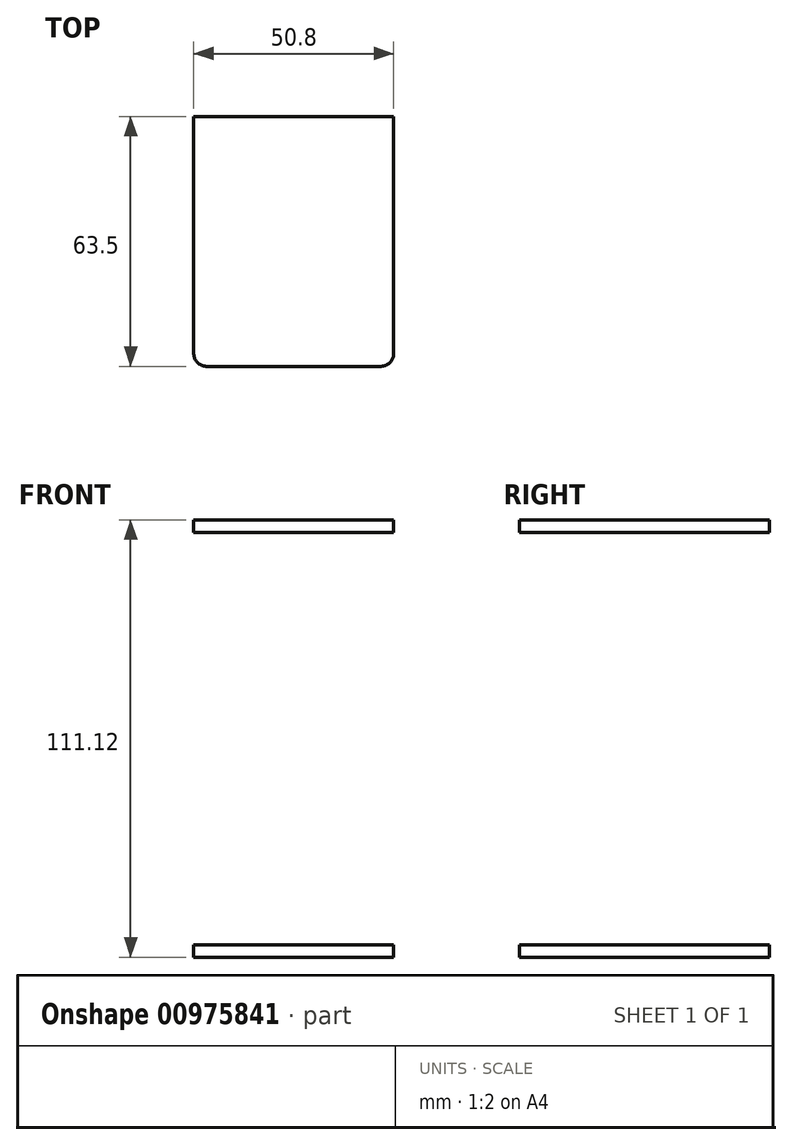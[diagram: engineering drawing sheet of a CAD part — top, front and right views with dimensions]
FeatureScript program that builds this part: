
annotation { "Feature Type Name" : "Feature", "Feature Type Description" : "" }
export const myFeature = defineFeature(function(context is Context, id is Id, definition is map)
    precondition{}
    {
        {
            var Q0;
            Q0=qCreatedBy(makeId("Front.planeOp"),FACE);
            var sketch = newSketch(context, id + "F0", { "sketchPlane" : qUnion([Q0])});
            skLineSegment(sketch, "E0.bottom", {"start": v(-72.27, 0) * mm, "end": v(-21.47, 0) * mm});
            skLineSegment(sketch, "E0.top", {"start": v(-72.27, -3.18) * mm, "end": v(-21.47, -3.18) * mm});
            skLineSegment(sketch, "E0.left", {"start": v(-72.27, 0) * mm, "end": v(-72.27, -3.18) * mm});
            skLineSegment(sketch, "E0.right", {"start": v(-21.47, 0) * mm, "end": v(-21.47, -3.18) * mm});
            skSolve(sketch);
        }
        {
            var Q0;
            Q0=qSketchRegion(id+"F0",true);
            extrude(context, id + "F1", {"entities" : qUnion([Q0]), "depth" : 63.5 * mm, "offsetDistance" : 25.4 * mm});
        }
        {
            var Q0;
            Q0=makeQuery(id+"F1.opExtrude","CAP_EDGE",EDGE,{"disambiguationData":[OSD([sQuery(id+"F0.wireOp",EDGE,"E0.right")])],"isStart":false});
            fillet(context, id + "F2", {"entities" : qUnion([Q0]), "radius" : 3.17 * mm, "tangentPropagation" : true, "allowEdgeOverflow" : false});
        }
        {
            var Q0;
            Q0=makeQuery(id+"F1.opExtrude","CAP_EDGE",EDGE,{"disambiguationData":[OSD([sQuery(id+"F0.wireOp",EDGE,"E0.left")])],"isStart":false});
            fillet(context, id + "F3", {"entities" : qUnion([Q0]), "radius" : 3.17 * mm, "tangentPropagation" : true, "allowEdgeOverflow" : false});
        }
        {
            var Q0;
            Q0=makeQuery(id+"F1.opExtrude","SWEPT_BODY",BODY,{"disambiguationData":[OSD([sQuery(id+"F0.wireOp",EDGE,"E0.bottom"),sQuery(id+"F0.wireOp",EDGE,"E0.top"),sQuery(id+"F0.wireOp",EDGE,"E0.left"),sQuery(id+"F0.wireOp",EDGE,"E0.right")])]});
            transform(context, id + "F4", {"entities" : qUnion([Q0]), "transformType" : TransformType.TRANSLATION_3D, "dx" : 76.2 * mm, "dy" : 0 * mm, "dz" : 0 * mm, "makeCopy" : true});
        }
        {
            var Q0;
            Q0=makeQuery(id+"F4.opPattern","COPY",BODY,{"derivedFrom":makeQuery(id+"F1.opExtrude","SWEPT_BODY",BODY,{"disambiguationData":[OSD([sQuery(id+"F0.wireOp",EDGE,"E0.bottom"),sQuery(id+"F0.wireOp",EDGE,"E0.top"),sQuery(id+"F0.wireOp",EDGE,"E0.left"),sQuery(id+"F0.wireOp",EDGE,"E0.right")])]}),"instanceName":"1"});
            transform(context, id + "F5", {"entities" : qUnion([Q0]), "transformType" : TransformType.TRANSLATION_3D, "dx" : 76.2 * mm, "dy" : 0 * mm, "dz" : 0 * mm, "makeCopy" : true});
        }
        {
            var Q0;
            Q0=makeQuery(id+"F5.opPattern","COPY",BODY,{"derivedFrom":makeQuery(id+"F4.opPattern","COPY",BODY,{"derivedFrom":makeQuery(id+"F1.opExtrude","SWEPT_BODY",BODY,{"disambiguationData":[OSD([sQuery(id+"F0.wireOp",EDGE,"E0.bottom"),sQuery(id+"F0.wireOp",EDGE,"E0.top"),sQuery(id+"F0.wireOp",EDGE,"E0.left"),sQuery(id+"F0.wireOp",EDGE,"E0.right")])]}),"instanceName":"1"}),"instanceName":"1"});
            transform(context, id + "F6", {"entities" : qUnion([Q0]), "transformType" : TransformType.TRANSLATION_3D, "dx" : 76.2 * mm, "dy" : 0 * mm, "dz" : 0 * mm, "makeCopy" : true});
        }
        {
            var Q0;
            Q0=makeQuery(id+"F6.opPattern","COPY",BODY,{"derivedFrom":makeQuery(id+"F5.opPattern","COPY",BODY,{"derivedFrom":makeQuery(id+"F4.opPattern","COPY",BODY,{"derivedFrom":makeQuery(id+"F1.opExtrude","SWEPT_BODY",BODY,{"disambiguationData":[OSD([sQuery(id+"F0.wireOp",EDGE,"E0.bottom"),sQuery(id+"F0.wireOp",EDGE,"E0.top"),sQuery(id+"F0.wireOp",EDGE,"E0.left"),sQuery(id+"F0.wireOp",EDGE,"E0.right")])]}),"instanceName":"1"}),"instanceName":"1"}),"instanceName":"1"});
            transform(context, id + "F7", {"entities" : qUnion([Q0]), "transformType" : TransformType.TRANSLATION_3D, "dx" : 76.2 * mm, "dy" : 0 * mm, "dz" : 0 * mm, "makeCopy" : true});
        }
        {
            var Q0;
            Q0=makeQuery(id+"F1.opExtrude","SWEPT_BODY",BODY,{"disambiguationData":[OSD([sQuery(id+"F0.wireOp",EDGE,"E0.bottom"),sQuery(id+"F0.wireOp",EDGE,"E0.top"),sQuery(id+"F0.wireOp",EDGE,"E0.left"),sQuery(id+"F0.wireOp",EDGE,"E0.right")])]});
            var Q1;
            Q1=makeQuery(id+"F4.opPattern","COPY",BODY,{"derivedFrom":makeQuery(id+"F1.opExtrude","SWEPT_BODY",BODY,{"disambiguationData":[OSD([sQuery(id+"F0.wireOp",EDGE,"E0.bottom"),sQuery(id+"F0.wireOp",EDGE,"E0.top"),sQuery(id+"F0.wireOp",EDGE,"E0.left"),sQuery(id+"F0.wireOp",EDGE,"E0.right")])]}),"instanceName":"1"});
            var Q2;
            Q2=makeQuery(id+"F5.opPattern","COPY",BODY,{"derivedFrom":makeQuery(id+"F4.opPattern","COPY",BODY,{"derivedFrom":makeQuery(id+"F1.opExtrude","SWEPT_BODY",BODY,{"disambiguationData":[OSD([sQuery(id+"F0.wireOp",EDGE,"E0.bottom"),sQuery(id+"F0.wireOp",EDGE,"E0.top"),sQuery(id+"F0.wireOp",EDGE,"E0.left"),sQuery(id+"F0.wireOp",EDGE,"E0.right")])]}),"instanceName":"1"}),"instanceName":"1"});
            var Q3;
            Q3=makeQuery(id+"F6.opPattern","COPY",BODY,{"derivedFrom":makeQuery(id+"F5.opPattern","COPY",BODY,{"derivedFrom":makeQuery(id+"F4.opPattern","COPY",BODY,{"derivedFrom":makeQuery(id+"F1.opExtrude","SWEPT_BODY",BODY,{"disambiguationData":[OSD([sQuery(id+"F0.wireOp",EDGE,"E0.bottom"),sQuery(id+"F0.wireOp",EDGE,"E0.top"),sQuery(id+"F0.wireOp",EDGE,"E0.left"),sQuery(id+"F0.wireOp",EDGE,"E0.right")])]}),"instanceName":"1"}),"instanceName":"1"}),"instanceName":"1"});
            var Q4;
            Q4=makeQuery(id+"F7.opPattern","COPY",BODY,{"derivedFrom":makeQuery(id+"F6.opPattern","COPY",BODY,{"derivedFrom":makeQuery(id+"F5.opPattern","COPY",BODY,{"derivedFrom":makeQuery(id+"F4.opPattern","COPY",BODY,{"derivedFrom":makeQuery(id+"F1.opExtrude","SWEPT_BODY",BODY,{"disambiguationData":[OSD([sQuery(id+"F0.wireOp",EDGE,"E0.bottom"),sQuery(id+"F0.wireOp",EDGE,"E0.top"),sQuery(id+"F0.wireOp",EDGE,"E0.left"),sQuery(id+"F0.wireOp",EDGE,"E0.right")])]}),"instanceName":"1"}),"instanceName":"1"}),"instanceName":"1"}),"instanceName":"1"});
            transform(context, id + "F8", {"entities" : qUnion([Q0, Q1, Q2, Q3, Q4]), "transformType" : TransformType.TRANSLATION_3D, "dx" : 0 * mm, "dy" : 0 * mm, "dz" : 104.77 * mm, "makeCopy" : true});
        }
        {
            var Q0;
            Q0=makeQuery(id+"F8.opPattern","COPY",BODY,{"derivedFrom":makeQuery(id+"F1.opExtrude","SWEPT_BODY",BODY,{"disambiguationData":[OSD([sQuery(id+"F0.wireOp",EDGE,"E0.bottom"),sQuery(id+"F0.wireOp",EDGE,"E0.top"),sQuery(id+"F0.wireOp",EDGE,"E0.left"),sQuery(id+"F0.wireOp",EDGE,"E0.right")])]}),"instanceName":"1"});
            var Q1;
            Q1=makeQuery(id+"F8.opPattern","COPY",BODY,{"derivedFrom":makeQuery(id+"F4.opPattern","COPY",BODY,{"derivedFrom":makeQuery(id+"F1.opExtrude","SWEPT_BODY",BODY,{"disambiguationData":[OSD([sQuery(id+"F0.wireOp",EDGE,"E0.bottom"),sQuery(id+"F0.wireOp",EDGE,"E0.top"),sQuery(id+"F0.wireOp",EDGE,"E0.left"),sQuery(id+"F0.wireOp",EDGE,"E0.right")])]}),"instanceName":"1"}),"instanceName":"1"});
            var Q2;
            Q2=makeQuery(id+"F8.opPattern","COPY",BODY,{"derivedFrom":makeQuery(id+"F6.opPattern","COPY",BODY,{"derivedFrom":makeQuery(id+"F5.opPattern","COPY",BODY,{"derivedFrom":makeQuery(id+"F4.opPattern","COPY",BODY,{"derivedFrom":makeQuery(id+"F1.opExtrude","SWEPT_BODY",BODY,{"disambiguationData":[OSD([sQuery(id+"F0.wireOp",EDGE,"E0.bottom"),sQuery(id+"F0.wireOp",EDGE,"E0.top"),sQuery(id+"F0.wireOp",EDGE,"E0.left"),sQuery(id+"F0.wireOp",EDGE,"E0.right")])]}),"instanceName":"1"}),"instanceName":"1"}),"instanceName":"1"}),"instanceName":"1"});
            var Q3;
            Q3=makeQuery(id+"F8.opPattern","COPY",BODY,{"derivedFrom":makeQuery(id+"F7.opPattern","COPY",BODY,{"derivedFrom":makeQuery(id+"F6.opPattern","COPY",BODY,{"derivedFrom":makeQuery(id+"F5.opPattern","COPY",BODY,{"derivedFrom":makeQuery(id+"F4.opPattern","COPY",BODY,{"derivedFrom":makeQuery(id+"F1.opExtrude","SWEPT_BODY",BODY,{"disambiguationData":[OSD([sQuery(id+"F0.wireOp",EDGE,"E0.bottom"),sQuery(id+"F0.wireOp",EDGE,"E0.top"),sQuery(id+"F0.wireOp",EDGE,"E0.left"),sQuery(id+"F0.wireOp",EDGE,"E0.right")])]}),"instanceName":"1"}),"instanceName":"1"}),"instanceName":"1"}),"instanceName":"1"}),"instanceName":"1"});
            var Q4;
            Q4=makeQuery(id+"F8.opPattern","COPY",BODY,{"derivedFrom":makeQuery(id+"F5.opPattern","COPY",BODY,{"derivedFrom":makeQuery(id+"F4.opPattern","COPY",BODY,{"derivedFrom":makeQuery(id+"F1.opExtrude","SWEPT_BODY",BODY,{"disambiguationData":[OSD([sQuery(id+"F0.wireOp",EDGE,"E0.bottom"),sQuery(id+"F0.wireOp",EDGE,"E0.top"),sQuery(id+"F0.wireOp",EDGE,"E0.left"),sQuery(id+"F0.wireOp",EDGE,"E0.right")])]}),"instanceName":"1"}),"instanceName":"1"}),"instanceName":"1"});
            transform(context, id + "F9", {"entities" : qUnion([Q0, Q1, Q2, Q3, Q4]), "transformType" : TransformType.TRANSLATION_3D, "dx" : 0 * mm, "dy" : 0 * mm, "dz" : 127 * mm, "makeCopy" : true});
        }
        {
            var Q0;
            Q0=makeQuery(id+"F9.opPattern","COPY",BODY,{"derivedFrom":makeQuery(id+"F8.opPattern","COPY",BODY,{"derivedFrom":makeQuery(id+"F1.opExtrude","SWEPT_BODY",BODY,{"disambiguationData":[OSD([sQuery(id+"F0.wireOp",EDGE,"E0.bottom"),sQuery(id+"F0.wireOp",EDGE,"E0.top"),sQuery(id+"F0.wireOp",EDGE,"E0.left"),sQuery(id+"F0.wireOp",EDGE,"E0.right")])]}),"instanceName":"1"}),"instanceName":"1"});
            var Q1;
            Q1=makeQuery(id+"F9.opPattern","COPY",BODY,{"derivedFrom":makeQuery(id+"F8.opPattern","COPY",BODY,{"derivedFrom":makeQuery(id+"F4.opPattern","COPY",BODY,{"derivedFrom":makeQuery(id+"F1.opExtrude","SWEPT_BODY",BODY,{"disambiguationData":[OSD([sQuery(id+"F0.wireOp",EDGE,"E0.bottom"),sQuery(id+"F0.wireOp",EDGE,"E0.top"),sQuery(id+"F0.wireOp",EDGE,"E0.left"),sQuery(id+"F0.wireOp",EDGE,"E0.right")])]}),"instanceName":"1"}),"instanceName":"1"}),"instanceName":"1"});
            var Q2;
            Q2=makeQuery(id+"F9.opPattern","COPY",BODY,{"derivedFrom":makeQuery(id+"F8.opPattern","COPY",BODY,{"derivedFrom":makeQuery(id+"F5.opPattern","COPY",BODY,{"derivedFrom":makeQuery(id+"F4.opPattern","COPY",BODY,{"derivedFrom":makeQuery(id+"F1.opExtrude","SWEPT_BODY",BODY,{"disambiguationData":[OSD([sQuery(id+"F0.wireOp",EDGE,"E0.bottom"),sQuery(id+"F0.wireOp",EDGE,"E0.top"),sQuery(id+"F0.wireOp",EDGE,"E0.left"),sQuery(id+"F0.wireOp",EDGE,"E0.right")])]}),"instanceName":"1"}),"instanceName":"1"}),"instanceName":"1"}),"instanceName":"1"});
            var Q3;
            Q3=makeQuery(id+"F9.opPattern","COPY",BODY,{"derivedFrom":makeQuery(id+"F8.opPattern","COPY",BODY,{"derivedFrom":makeQuery(id+"F6.opPattern","COPY",BODY,{"derivedFrom":makeQuery(id+"F5.opPattern","COPY",BODY,{"derivedFrom":makeQuery(id+"F4.opPattern","COPY",BODY,{"derivedFrom":makeQuery(id+"F1.opExtrude","SWEPT_BODY",BODY,{"disambiguationData":[OSD([sQuery(id+"F0.wireOp",EDGE,"E0.bottom"),sQuery(id+"F0.wireOp",EDGE,"E0.top"),sQuery(id+"F0.wireOp",EDGE,"E0.left"),sQuery(id+"F0.wireOp",EDGE,"E0.right")])]}),"instanceName":"1"}),"instanceName":"1"}),"instanceName":"1"}),"instanceName":"1"}),"instanceName":"1"});
            var Q4;
            Q4=makeQuery(id+"F9.opPattern","COPY",BODY,{"derivedFrom":makeQuery(id+"F8.opPattern","COPY",BODY,{"derivedFrom":makeQuery(id+"F7.opPattern","COPY",BODY,{"derivedFrom":makeQuery(id+"F6.opPattern","COPY",BODY,{"derivedFrom":makeQuery(id+"F5.opPattern","COPY",BODY,{"derivedFrom":makeQuery(id+"F4.opPattern","COPY",BODY,{"derivedFrom":makeQuery(id+"F1.opExtrude","SWEPT_BODY",BODY,{"disambiguationData":[OSD([sQuery(id+"F0.wireOp",EDGE,"E0.bottom"),sQuery(id+"F0.wireOp",EDGE,"E0.top"),sQuery(id+"F0.wireOp",EDGE,"E0.left"),sQuery(id+"F0.wireOp",EDGE,"E0.right")])]}),"instanceName":"1"}),"instanceName":"1"}),"instanceName":"1"}),"instanceName":"1"}),"instanceName":"1"}),"instanceName":"1"});
            transform(context, id + "F10", {"entities" : qUnion([Q0, Q1, Q2, Q3, Q4]), "transformType" : TransformType.TRANSLATION_3D, "dx" : 0 * mm, "dy" : 0 * mm, "dz" : 104.77 * mm, "makeCopy" : true});
        }
        {
            var Q0;
            Q0=makeQuery(id+"F10.opPattern","COPY",BODY,{"derivedFrom":makeQuery(id+"F9.opPattern","COPY",BODY,{"derivedFrom":makeQuery(id+"F8.opPattern","COPY",BODY,{"derivedFrom":makeQuery(id+"F1.opExtrude","SWEPT_BODY",BODY,{"disambiguationData":[OSD([sQuery(id+"F0.wireOp",EDGE,"E0.bottom"),sQuery(id+"F0.wireOp",EDGE,"E0.top"),sQuery(id+"F0.wireOp",EDGE,"E0.left"),sQuery(id+"F0.wireOp",EDGE,"E0.right")])]}),"instanceName":"1"}),"instanceName":"1"}),"instanceName":"1"});
            var Q1;
            Q1=makeQuery(id+"F10.opPattern","COPY",BODY,{"derivedFrom":makeQuery(id+"F9.opPattern","COPY",BODY,{"derivedFrom":makeQuery(id+"F8.opPattern","COPY",BODY,{"derivedFrom":makeQuery(id+"F4.opPattern","COPY",BODY,{"derivedFrom":makeQuery(id+"F1.opExtrude","SWEPT_BODY",BODY,{"disambiguationData":[OSD([sQuery(id+"F0.wireOp",EDGE,"E0.bottom"),sQuery(id+"F0.wireOp",EDGE,"E0.top"),sQuery(id+"F0.wireOp",EDGE,"E0.left"),sQuery(id+"F0.wireOp",EDGE,"E0.right")])]}),"instanceName":"1"}),"instanceName":"1"}),"instanceName":"1"}),"instanceName":"1"});
            var Q2;
            Q2=makeQuery(id+"F10.opPattern","COPY",BODY,{"derivedFrom":makeQuery(id+"F9.opPattern","COPY",BODY,{"derivedFrom":makeQuery(id+"F8.opPattern","COPY",BODY,{"derivedFrom":makeQuery(id+"F5.opPattern","COPY",BODY,{"derivedFrom":makeQuery(id+"F4.opPattern","COPY",BODY,{"derivedFrom":makeQuery(id+"F1.opExtrude","SWEPT_BODY",BODY,{"disambiguationData":[OSD([sQuery(id+"F0.wireOp",EDGE,"E0.bottom"),sQuery(id+"F0.wireOp",EDGE,"E0.top"),sQuery(id+"F0.wireOp",EDGE,"E0.left"),sQuery(id+"F0.wireOp",EDGE,"E0.right")])]}),"instanceName":"1"}),"instanceName":"1"}),"instanceName":"1"}),"instanceName":"1"}),"instanceName":"1"});
            var Q3;
            Q3=makeQuery(id+"F10.opPattern","COPY",BODY,{"derivedFrom":makeQuery(id+"F9.opPattern","COPY",BODY,{"derivedFrom":makeQuery(id+"F8.opPattern","COPY",BODY,{"derivedFrom":makeQuery(id+"F6.opPattern","COPY",BODY,{"derivedFrom":makeQuery(id+"F5.opPattern","COPY",BODY,{"derivedFrom":makeQuery(id+"F4.opPattern","COPY",BODY,{"derivedFrom":makeQuery(id+"F1.opExtrude","SWEPT_BODY",BODY,{"disambiguationData":[OSD([sQuery(id+"F0.wireOp",EDGE,"E0.bottom"),sQuery(id+"F0.wireOp",EDGE,"E0.top"),sQuery(id+"F0.wireOp",EDGE,"E0.left"),sQuery(id+"F0.wireOp",EDGE,"E0.right")])]}),"instanceName":"1"}),"instanceName":"1"}),"instanceName":"1"}),"instanceName":"1"}),"instanceName":"1"}),"instanceName":"1"});
            var Q4;
            Q4=makeQuery(id+"F10.opPattern","COPY",BODY,{"derivedFrom":makeQuery(id+"F9.opPattern","COPY",BODY,{"derivedFrom":makeQuery(id+"F8.opPattern","COPY",BODY,{"derivedFrom":makeQuery(id+"F7.opPattern","COPY",BODY,{"derivedFrom":makeQuery(id+"F6.opPattern","COPY",BODY,{"derivedFrom":makeQuery(id+"F5.opPattern","COPY",BODY,{"derivedFrom":makeQuery(id+"F4.opPattern","COPY",BODY,{"derivedFrom":makeQuery(id+"F1.opExtrude","SWEPT_BODY",BODY,{"disambiguationData":[OSD([sQuery(id+"F0.wireOp",EDGE,"E0.bottom"),sQuery(id+"F0.wireOp",EDGE,"E0.top"),sQuery(id+"F0.wireOp",EDGE,"E0.left"),sQuery(id+"F0.wireOp",EDGE,"E0.right")])]}),"instanceName":"1"}),"instanceName":"1"}),"instanceName":"1"}),"instanceName":"1"}),"instanceName":"1"}),"instanceName":"1"}),"instanceName":"1"});
            transform(context, id + "F11", {"entities" : qUnion([Q0, Q1, Q2, Q3, Q4]), "transformType" : TransformType.TRANSLATION_3D, "dx" : 0 * mm, "dy" : 0 * mm, "dz" : 104.77 * mm, "makeCopy" : true});
        }
        {
            var Q0;
            Q0=makeQuery(id+"F10.opPattern","COPY",BODY,{"derivedFrom":makeQuery(id+"F9.opPattern","COPY",BODY,{"derivedFrom":makeQuery(id+"F8.opPattern","COPY",BODY,{"derivedFrom":makeQuery(id+"F7.opPattern","COPY",BODY,{"derivedFrom":makeQuery(id+"F6.opPattern","COPY",BODY,{"derivedFrom":makeQuery(id+"F5.opPattern","COPY",BODY,{"derivedFrom":makeQuery(id+"F4.opPattern","COPY",BODY,{"derivedFrom":makeQuery(id+"F1.opExtrude","SWEPT_BODY",BODY,{"disambiguationData":[OSD([sQuery(id+"F0.wireOp",EDGE,"E0.bottom"),sQuery(id+"F0.wireOp",EDGE,"E0.top"),sQuery(id+"F0.wireOp",EDGE,"E0.left"),sQuery(id+"F0.wireOp",EDGE,"E0.right")])]}),"instanceName":"1"}),"instanceName":"1"}),"instanceName":"1"}),"instanceName":"1"}),"instanceName":"1"}),"instanceName":"1"}),"instanceName":"1"});
            var Q1;
            Q1=makeQuery(id+"F10.opPattern","COPY",BODY,{"derivedFrom":makeQuery(id+"F9.opPattern","COPY",BODY,{"derivedFrom":makeQuery(id+"F8.opPattern","COPY",BODY,{"derivedFrom":makeQuery(id+"F6.opPattern","COPY",BODY,{"derivedFrom":makeQuery(id+"F5.opPattern","COPY",BODY,{"derivedFrom":makeQuery(id+"F4.opPattern","COPY",BODY,{"derivedFrom":makeQuery(id+"F1.opExtrude","SWEPT_BODY",BODY,{"disambiguationData":[OSD([sQuery(id+"F0.wireOp",EDGE,"E0.bottom"),sQuery(id+"F0.wireOp",EDGE,"E0.top"),sQuery(id+"F0.wireOp",EDGE,"E0.left"),sQuery(id+"F0.wireOp",EDGE,"E0.right")])]}),"instanceName":"1"}),"instanceName":"1"}),"instanceName":"1"}),"instanceName":"1"}),"instanceName":"1"}),"instanceName":"1"});
            var Q2;
            Q2=makeQuery(id+"F10.opPattern","COPY",BODY,{"derivedFrom":makeQuery(id+"F9.opPattern","COPY",BODY,{"derivedFrom":makeQuery(id+"F8.opPattern","COPY",BODY,{"derivedFrom":makeQuery(id+"F5.opPattern","COPY",BODY,{"derivedFrom":makeQuery(id+"F4.opPattern","COPY",BODY,{"derivedFrom":makeQuery(id+"F1.opExtrude","SWEPT_BODY",BODY,{"disambiguationData":[OSD([sQuery(id+"F0.wireOp",EDGE,"E0.bottom"),sQuery(id+"F0.wireOp",EDGE,"E0.top"),sQuery(id+"F0.wireOp",EDGE,"E0.left"),sQuery(id+"F0.wireOp",EDGE,"E0.right")])]}),"instanceName":"1"}),"instanceName":"1"}),"instanceName":"1"}),"instanceName":"1"}),"instanceName":"1"});
            var Q3;
            Q3=makeQuery(id+"F10.opPattern","COPY",BODY,{"derivedFrom":makeQuery(id+"F9.opPattern","COPY",BODY,{"derivedFrom":makeQuery(id+"F8.opPattern","COPY",BODY,{"derivedFrom":makeQuery(id+"F4.opPattern","COPY",BODY,{"derivedFrom":makeQuery(id+"F1.opExtrude","SWEPT_BODY",BODY,{"disambiguationData":[OSD([sQuery(id+"F0.wireOp",EDGE,"E0.bottom"),sQuery(id+"F0.wireOp",EDGE,"E0.top"),sQuery(id+"F0.wireOp",EDGE,"E0.left"),sQuery(id+"F0.wireOp",EDGE,"E0.right")])]}),"instanceName":"1"}),"instanceName":"1"}),"instanceName":"1"}),"instanceName":"1"});
            var Q4;
            Q4=makeQuery(id+"F10.opPattern","COPY",BODY,{"derivedFrom":makeQuery(id+"F9.opPattern","COPY",BODY,{"derivedFrom":makeQuery(id+"F8.opPattern","COPY",BODY,{"derivedFrom":makeQuery(id+"F1.opExtrude","SWEPT_BODY",BODY,{"disambiguationData":[OSD([sQuery(id+"F0.wireOp",EDGE,"E0.bottom"),sQuery(id+"F0.wireOp",EDGE,"E0.top"),sQuery(id+"F0.wireOp",EDGE,"E0.left"),sQuery(id+"F0.wireOp",EDGE,"E0.right")])]}),"instanceName":"1"}),"instanceName":"1"}),"instanceName":"1"});
            var Q5;
            Q5=makeQuery(id+"F9.opPattern","COPY",BODY,{"derivedFrom":makeQuery(id+"F8.opPattern","COPY",BODY,{"derivedFrom":makeQuery(id+"F1.opExtrude","SWEPT_BODY",BODY,{"disambiguationData":[OSD([sQuery(id+"F0.wireOp",EDGE,"E0.bottom"),sQuery(id+"F0.wireOp",EDGE,"E0.top"),sQuery(id+"F0.wireOp",EDGE,"E0.left"),sQuery(id+"F0.wireOp",EDGE,"E0.right")])]}),"instanceName":"1"}),"instanceName":"1"});
            var Q6;
            Q6=makeQuery(id+"F9.opPattern","COPY",BODY,{"derivedFrom":makeQuery(id+"F8.opPattern","COPY",BODY,{"derivedFrom":makeQuery(id+"F4.opPattern","COPY",BODY,{"derivedFrom":makeQuery(id+"F1.opExtrude","SWEPT_BODY",BODY,{"disambiguationData":[OSD([sQuery(id+"F0.wireOp",EDGE,"E0.bottom"),sQuery(id+"F0.wireOp",EDGE,"E0.top"),sQuery(id+"F0.wireOp",EDGE,"E0.left"),sQuery(id+"F0.wireOp",EDGE,"E0.right")])]}),"instanceName":"1"}),"instanceName":"1"}),"instanceName":"1"});
            var Q7;
            Q7=makeQuery(id+"F9.opPattern","COPY",BODY,{"derivedFrom":makeQuery(id+"F8.opPattern","COPY",BODY,{"derivedFrom":makeQuery(id+"F6.opPattern","COPY",BODY,{"derivedFrom":makeQuery(id+"F5.opPattern","COPY",BODY,{"derivedFrom":makeQuery(id+"F4.opPattern","COPY",BODY,{"derivedFrom":makeQuery(id+"F1.opExtrude","SWEPT_BODY",BODY,{"disambiguationData":[OSD([sQuery(id+"F0.wireOp",EDGE,"E0.bottom"),sQuery(id+"F0.wireOp",EDGE,"E0.top"),sQuery(id+"F0.wireOp",EDGE,"E0.left"),sQuery(id+"F0.wireOp",EDGE,"E0.right")])]}),"instanceName":"1"}),"instanceName":"1"}),"instanceName":"1"}),"instanceName":"1"}),"instanceName":"1"});
            var Q8;
            Q8=makeQuery(id+"F9.opPattern","COPY",BODY,{"derivedFrom":makeQuery(id+"F8.opPattern","COPY",BODY,{"derivedFrom":makeQuery(id+"F7.opPattern","COPY",BODY,{"derivedFrom":makeQuery(id+"F6.opPattern","COPY",BODY,{"derivedFrom":makeQuery(id+"F5.opPattern","COPY",BODY,{"derivedFrom":makeQuery(id+"F4.opPattern","COPY",BODY,{"derivedFrom":makeQuery(id+"F1.opExtrude","SWEPT_BODY",BODY,{"disambiguationData":[OSD([sQuery(id+"F0.wireOp",EDGE,"E0.bottom"),sQuery(id+"F0.wireOp",EDGE,"E0.top"),sQuery(id+"F0.wireOp",EDGE,"E0.left"),sQuery(id+"F0.wireOp",EDGE,"E0.right")])]}),"instanceName":"1"}),"instanceName":"1"}),"instanceName":"1"}),"instanceName":"1"}),"instanceName":"1"}),"instanceName":"1"});
            var Q9;
            Q9=makeQuery(id+"F9.opPattern","COPY",BODY,{"derivedFrom":makeQuery(id+"F8.opPattern","COPY",BODY,{"derivedFrom":makeQuery(id+"F5.opPattern","COPY",BODY,{"derivedFrom":makeQuery(id+"F4.opPattern","COPY",BODY,{"derivedFrom":makeQuery(id+"F1.opExtrude","SWEPT_BODY",BODY,{"disambiguationData":[OSD([sQuery(id+"F0.wireOp",EDGE,"E0.bottom"),sQuery(id+"F0.wireOp",EDGE,"E0.top"),sQuery(id+"F0.wireOp",EDGE,"E0.left"),sQuery(id+"F0.wireOp",EDGE,"E0.right")])]}),"instanceName":"1"}),"instanceName":"1"}),"instanceName":"1"}),"instanceName":"1"});
            transform(context, id + "F12", {"entities" : qUnion([Q0, Q1, Q2, Q3, Q4, Q5, Q6, Q7, Q8, Q9]), "transformType" : TransformType.TRANSLATION_3D, "dx" : 0 * mm, "dy" : 0 * mm, "dz" : -3.17 * mm, "makeCopy" : false});
        }
        {
            var Q0;
            Q0=makeQuery(id+"F8.opPattern","COPY",BODY,{"derivedFrom":makeQuery(id+"F1.opExtrude","SWEPT_BODY",BODY,{"disambiguationData":[OSD([sQuery(id+"F0.wireOp",EDGE,"E0.bottom"),sQuery(id+"F0.wireOp",EDGE,"E0.top"),sQuery(id+"F0.wireOp",EDGE,"E0.left"),sQuery(id+"F0.wireOp",EDGE,"E0.right")])]}),"instanceName":"1"});
            var Q1;
            Q1=makeQuery(id+"F11.opPattern","COPY",BODY,{"derivedFrom":makeQuery(id+"F10.opPattern","COPY",BODY,{"derivedFrom":makeQuery(id+"F9.opPattern","COPY",BODY,{"derivedFrom":makeQuery(id+"F8.opPattern","COPY",BODY,{"derivedFrom":makeQuery(id+"F7.opPattern","COPY",BODY,{"derivedFrom":makeQuery(id+"F6.opPattern","COPY",BODY,{"derivedFrom":makeQuery(id+"F5.opPattern","COPY",BODY,{"derivedFrom":makeQuery(id+"F4.opPattern","COPY",BODY,{"derivedFrom":makeQuery(id+"F1.opExtrude","SWEPT_BODY",BODY,{"disambiguationData":[OSD([sQuery(id+"F0.wireOp",EDGE,"E0.bottom"),sQuery(id+"F0.wireOp",EDGE,"E0.top"),sQuery(id+"F0.wireOp",EDGE,"E0.left"),sQuery(id+"F0.wireOp",EDGE,"E0.right")])]}),"instanceName":"1"}),"instanceName":"1"}),"instanceName":"1"}),"instanceName":"1"}),"instanceName":"1"}),"instanceName":"1"}),"instanceName":"1"}),"instanceName":"1"});
            var Q2;
            Q2=makeQuery(id+"F8.opPattern","COPY",BODY,{"derivedFrom":makeQuery(id+"F4.opPattern","COPY",BODY,{"derivedFrom":makeQuery(id+"F1.opExtrude","SWEPT_BODY",BODY,{"disambiguationData":[OSD([sQuery(id+"F0.wireOp",EDGE,"E0.bottom"),sQuery(id+"F0.wireOp",EDGE,"E0.top"),sQuery(id+"F0.wireOp",EDGE,"E0.left"),sQuery(id+"F0.wireOp",EDGE,"E0.right")])]}),"instanceName":"1"}),"instanceName":"1"});
            var Q3;
            Q3=makeQuery(id+"F8.opPattern","COPY",BODY,{"derivedFrom":makeQuery(id+"F5.opPattern","COPY",BODY,{"derivedFrom":makeQuery(id+"F4.opPattern","COPY",BODY,{"derivedFrom":makeQuery(id+"F1.opExtrude","SWEPT_BODY",BODY,{"disambiguationData":[OSD([sQuery(id+"F0.wireOp",EDGE,"E0.bottom"),sQuery(id+"F0.wireOp",EDGE,"E0.top"),sQuery(id+"F0.wireOp",EDGE,"E0.left"),sQuery(id+"F0.wireOp",EDGE,"E0.right")])]}),"instanceName":"1"}),"instanceName":"1"}),"instanceName":"1"});
            var Q4;
            Q4=makeQuery(id+"F8.opPattern","COPY",BODY,{"derivedFrom":makeQuery(id+"F6.opPattern","COPY",BODY,{"derivedFrom":makeQuery(id+"F5.opPattern","COPY",BODY,{"derivedFrom":makeQuery(id+"F4.opPattern","COPY",BODY,{"derivedFrom":makeQuery(id+"F1.opExtrude","SWEPT_BODY",BODY,{"disambiguationData":[OSD([sQuery(id+"F0.wireOp",EDGE,"E0.bottom"),sQuery(id+"F0.wireOp",EDGE,"E0.top"),sQuery(id+"F0.wireOp",EDGE,"E0.left"),sQuery(id+"F0.wireOp",EDGE,"E0.right")])]}),"instanceName":"1"}),"instanceName":"1"}),"instanceName":"1"}),"instanceName":"1"});
            var Q5;
            Q5=makeQuery(id+"F8.opPattern","COPY",BODY,{"derivedFrom":makeQuery(id+"F7.opPattern","COPY",BODY,{"derivedFrom":makeQuery(id+"F6.opPattern","COPY",BODY,{"derivedFrom":makeQuery(id+"F5.opPattern","COPY",BODY,{"derivedFrom":makeQuery(id+"F4.opPattern","COPY",BODY,{"derivedFrom":makeQuery(id+"F1.opExtrude","SWEPT_BODY",BODY,{"disambiguationData":[OSD([sQuery(id+"F0.wireOp",EDGE,"E0.bottom"),sQuery(id+"F0.wireOp",EDGE,"E0.top"),sQuery(id+"F0.wireOp",EDGE,"E0.left"),sQuery(id+"F0.wireOp",EDGE,"E0.right")])]}),"instanceName":"1"}),"instanceName":"1"}),"instanceName":"1"}),"instanceName":"1"}),"instanceName":"1"});
            var Q6;
            Q6=makeQuery(id+"F9.opPattern","COPY",BODY,{"derivedFrom":makeQuery(id+"F8.opPattern","COPY",BODY,{"derivedFrom":makeQuery(id+"F1.opExtrude","SWEPT_BODY",BODY,{"disambiguationData":[OSD([sQuery(id+"F0.wireOp",EDGE,"E0.bottom"),sQuery(id+"F0.wireOp",EDGE,"E0.top"),sQuery(id+"F0.wireOp",EDGE,"E0.left"),sQuery(id+"F0.wireOp",EDGE,"E0.right")])]}),"instanceName":"1"}),"instanceName":"1"});
            var Q7;
            Q7=makeQuery(id+"F9.opPattern","COPY",BODY,{"derivedFrom":makeQuery(id+"F8.opPattern","COPY",BODY,{"derivedFrom":makeQuery(id+"F4.opPattern","COPY",BODY,{"derivedFrom":makeQuery(id+"F1.opExtrude","SWEPT_BODY",BODY,{"disambiguationData":[OSD([sQuery(id+"F0.wireOp",EDGE,"E0.bottom"),sQuery(id+"F0.wireOp",EDGE,"E0.top"),sQuery(id+"F0.wireOp",EDGE,"E0.left"),sQuery(id+"F0.wireOp",EDGE,"E0.right")])]}),"instanceName":"1"}),"instanceName":"1"}),"instanceName":"1"});
            var Q8;
            Q8=makeQuery(id+"F9.opPattern","COPY",BODY,{"derivedFrom":makeQuery(id+"F8.opPattern","COPY",BODY,{"derivedFrom":makeQuery(id+"F5.opPattern","COPY",BODY,{"derivedFrom":makeQuery(id+"F4.opPattern","COPY",BODY,{"derivedFrom":makeQuery(id+"F1.opExtrude","SWEPT_BODY",BODY,{"disambiguationData":[OSD([sQuery(id+"F0.wireOp",EDGE,"E0.bottom"),sQuery(id+"F0.wireOp",EDGE,"E0.top"),sQuery(id+"F0.wireOp",EDGE,"E0.left"),sQuery(id+"F0.wireOp",EDGE,"E0.right")])]}),"instanceName":"1"}),"instanceName":"1"}),"instanceName":"1"}),"instanceName":"1"});
            var Q9;
            Q9=makeQuery(id+"F9.opPattern","COPY",BODY,{"derivedFrom":makeQuery(id+"F8.opPattern","COPY",BODY,{"derivedFrom":makeQuery(id+"F6.opPattern","COPY",BODY,{"derivedFrom":makeQuery(id+"F5.opPattern","COPY",BODY,{"derivedFrom":makeQuery(id+"F4.opPattern","COPY",BODY,{"derivedFrom":makeQuery(id+"F1.opExtrude","SWEPT_BODY",BODY,{"disambiguationData":[OSD([sQuery(id+"F0.wireOp",EDGE,"E0.bottom"),sQuery(id+"F0.wireOp",EDGE,"E0.top"),sQuery(id+"F0.wireOp",EDGE,"E0.left"),sQuery(id+"F0.wireOp",EDGE,"E0.right")])]}),"instanceName":"1"}),"instanceName":"1"}),"instanceName":"1"}),"instanceName":"1"}),"instanceName":"1"});
            var Q10;
            Q10=makeQuery(id+"F9.opPattern","COPY",BODY,{"derivedFrom":makeQuery(id+"F8.opPattern","COPY",BODY,{"derivedFrom":makeQuery(id+"F7.opPattern","COPY",BODY,{"derivedFrom":makeQuery(id+"F6.opPattern","COPY",BODY,{"derivedFrom":makeQuery(id+"F5.opPattern","COPY",BODY,{"derivedFrom":makeQuery(id+"F4.opPattern","COPY",BODY,{"derivedFrom":makeQuery(id+"F1.opExtrude","SWEPT_BODY",BODY,{"disambiguationData":[OSD([sQuery(id+"F0.wireOp",EDGE,"E0.bottom"),sQuery(id+"F0.wireOp",EDGE,"E0.top"),sQuery(id+"F0.wireOp",EDGE,"E0.left"),sQuery(id+"F0.wireOp",EDGE,"E0.right")])]}),"instanceName":"1"}),"instanceName":"1"}),"instanceName":"1"}),"instanceName":"1"}),"instanceName":"1"}),"instanceName":"1"});
            var Q11;
            Q11=makeQuery(id+"F10.opPattern","COPY",BODY,{"derivedFrom":makeQuery(id+"F9.opPattern","COPY",BODY,{"derivedFrom":makeQuery(id+"F8.opPattern","COPY",BODY,{"derivedFrom":makeQuery(id+"F1.opExtrude","SWEPT_BODY",BODY,{"disambiguationData":[OSD([sQuery(id+"F0.wireOp",EDGE,"E0.bottom"),sQuery(id+"F0.wireOp",EDGE,"E0.top"),sQuery(id+"F0.wireOp",EDGE,"E0.left"),sQuery(id+"F0.wireOp",EDGE,"E0.right")])]}),"instanceName":"1"}),"instanceName":"1"}),"instanceName":"1"});
            var Q12;
            Q12=makeQuery(id+"F10.opPattern","COPY",BODY,{"derivedFrom":makeQuery(id+"F9.opPattern","COPY",BODY,{"derivedFrom":makeQuery(id+"F8.opPattern","COPY",BODY,{"derivedFrom":makeQuery(id+"F4.opPattern","COPY",BODY,{"derivedFrom":makeQuery(id+"F1.opExtrude","SWEPT_BODY",BODY,{"disambiguationData":[OSD([sQuery(id+"F0.wireOp",EDGE,"E0.bottom"),sQuery(id+"F0.wireOp",EDGE,"E0.top"),sQuery(id+"F0.wireOp",EDGE,"E0.left"),sQuery(id+"F0.wireOp",EDGE,"E0.right")])]}),"instanceName":"1"}),"instanceName":"1"}),"instanceName":"1"}),"instanceName":"1"});
            var Q13;
            Q13=makeQuery(id+"F10.opPattern","COPY",BODY,{"derivedFrom":makeQuery(id+"F9.opPattern","COPY",BODY,{"derivedFrom":makeQuery(id+"F8.opPattern","COPY",BODY,{"derivedFrom":makeQuery(id+"F5.opPattern","COPY",BODY,{"derivedFrom":makeQuery(id+"F4.opPattern","COPY",BODY,{"derivedFrom":makeQuery(id+"F1.opExtrude","SWEPT_BODY",BODY,{"disambiguationData":[OSD([sQuery(id+"F0.wireOp",EDGE,"E0.bottom"),sQuery(id+"F0.wireOp",EDGE,"E0.top"),sQuery(id+"F0.wireOp",EDGE,"E0.left"),sQuery(id+"F0.wireOp",EDGE,"E0.right")])]}),"instanceName":"1"}),"instanceName":"1"}),"instanceName":"1"}),"instanceName":"1"}),"instanceName":"1"});
            var Q14;
            Q14=makeQuery(id+"F10.opPattern","COPY",BODY,{"derivedFrom":makeQuery(id+"F9.opPattern","COPY",BODY,{"derivedFrom":makeQuery(id+"F8.opPattern","COPY",BODY,{"derivedFrom":makeQuery(id+"F6.opPattern","COPY",BODY,{"derivedFrom":makeQuery(id+"F5.opPattern","COPY",BODY,{"derivedFrom":makeQuery(id+"F4.opPattern","COPY",BODY,{"derivedFrom":makeQuery(id+"F1.opExtrude","SWEPT_BODY",BODY,{"disambiguationData":[OSD([sQuery(id+"F0.wireOp",EDGE,"E0.bottom"),sQuery(id+"F0.wireOp",EDGE,"E0.top"),sQuery(id+"F0.wireOp",EDGE,"E0.left"),sQuery(id+"F0.wireOp",EDGE,"E0.right")])]}),"instanceName":"1"}),"instanceName":"1"}),"instanceName":"1"}),"instanceName":"1"}),"instanceName":"1"}),"instanceName":"1"});
            var Q15;
            Q15=makeQuery(id+"F10.opPattern","COPY",BODY,{"derivedFrom":makeQuery(id+"F9.opPattern","COPY",BODY,{"derivedFrom":makeQuery(id+"F8.opPattern","COPY",BODY,{"derivedFrom":makeQuery(id+"F7.opPattern","COPY",BODY,{"derivedFrom":makeQuery(id+"F6.opPattern","COPY",BODY,{"derivedFrom":makeQuery(id+"F5.opPattern","COPY",BODY,{"derivedFrom":makeQuery(id+"F4.opPattern","COPY",BODY,{"derivedFrom":makeQuery(id+"F1.opExtrude","SWEPT_BODY",BODY,{"disambiguationData":[OSD([sQuery(id+"F0.wireOp",EDGE,"E0.bottom"),sQuery(id+"F0.wireOp",EDGE,"E0.top"),sQuery(id+"F0.wireOp",EDGE,"E0.left"),sQuery(id+"F0.wireOp",EDGE,"E0.right")])]}),"instanceName":"1"}),"instanceName":"1"}),"instanceName":"1"}),"instanceName":"1"}),"instanceName":"1"}),"instanceName":"1"}),"instanceName":"1"});
            var Q16;
            Q16=makeQuery(id+"F11.opPattern","COPY",BODY,{"derivedFrom":makeQuery(id+"F10.opPattern","COPY",BODY,{"derivedFrom":makeQuery(id+"F9.opPattern","COPY",BODY,{"derivedFrom":makeQuery(id+"F8.opPattern","COPY",BODY,{"derivedFrom":makeQuery(id+"F1.opExtrude","SWEPT_BODY",BODY,{"disambiguationData":[OSD([sQuery(id+"F0.wireOp",EDGE,"E0.bottom"),sQuery(id+"F0.wireOp",EDGE,"E0.top"),sQuery(id+"F0.wireOp",EDGE,"E0.left"),sQuery(id+"F0.wireOp",EDGE,"E0.right")])]}),"instanceName":"1"}),"instanceName":"1"}),"instanceName":"1"}),"instanceName":"1"});
            var Q17;
            Q17=makeQuery(id+"F11.opPattern","COPY",BODY,{"derivedFrom":makeQuery(id+"F10.opPattern","COPY",BODY,{"derivedFrom":makeQuery(id+"F9.opPattern","COPY",BODY,{"derivedFrom":makeQuery(id+"F8.opPattern","COPY",BODY,{"derivedFrom":makeQuery(id+"F4.opPattern","COPY",BODY,{"derivedFrom":makeQuery(id+"F1.opExtrude","SWEPT_BODY",BODY,{"disambiguationData":[OSD([sQuery(id+"F0.wireOp",EDGE,"E0.bottom"),sQuery(id+"F0.wireOp",EDGE,"E0.top"),sQuery(id+"F0.wireOp",EDGE,"E0.left"),sQuery(id+"F0.wireOp",EDGE,"E0.right")])]}),"instanceName":"1"}),"instanceName":"1"}),"instanceName":"1"}),"instanceName":"1"}),"instanceName":"1"});
            var Q18;
            Q18=makeQuery(id+"F11.opPattern","COPY",BODY,{"derivedFrom":makeQuery(id+"F10.opPattern","COPY",BODY,{"derivedFrom":makeQuery(id+"F9.opPattern","COPY",BODY,{"derivedFrom":makeQuery(id+"F8.opPattern","COPY",BODY,{"derivedFrom":makeQuery(id+"F5.opPattern","COPY",BODY,{"derivedFrom":makeQuery(id+"F4.opPattern","COPY",BODY,{"derivedFrom":makeQuery(id+"F1.opExtrude","SWEPT_BODY",BODY,{"disambiguationData":[OSD([sQuery(id+"F0.wireOp",EDGE,"E0.bottom"),sQuery(id+"F0.wireOp",EDGE,"E0.top"),sQuery(id+"F0.wireOp",EDGE,"E0.left"),sQuery(id+"F0.wireOp",EDGE,"E0.right")])]}),"instanceName":"1"}),"instanceName":"1"}),"instanceName":"1"}),"instanceName":"1"}),"instanceName":"1"}),"instanceName":"1"});
            var Q19;
            Q19=makeQuery(id+"F11.opPattern","COPY",BODY,{"derivedFrom":makeQuery(id+"F10.opPattern","COPY",BODY,{"derivedFrom":makeQuery(id+"F9.opPattern","COPY",BODY,{"derivedFrom":makeQuery(id+"F8.opPattern","COPY",BODY,{"derivedFrom":makeQuery(id+"F6.opPattern","COPY",BODY,{"derivedFrom":makeQuery(id+"F5.opPattern","COPY",BODY,{"derivedFrom":makeQuery(id+"F4.opPattern","COPY",BODY,{"derivedFrom":makeQuery(id+"F1.opExtrude","SWEPT_BODY",BODY,{"disambiguationData":[OSD([sQuery(id+"F0.wireOp",EDGE,"E0.bottom"),sQuery(id+"F0.wireOp",EDGE,"E0.top"),sQuery(id+"F0.wireOp",EDGE,"E0.left"),sQuery(id+"F0.wireOp",EDGE,"E0.right")])]}),"instanceName":"1"}),"instanceName":"1"}),"instanceName":"1"}),"instanceName":"1"}),"instanceName":"1"}),"instanceName":"1"}),"instanceName":"1"});
            deleteBodies(context, id + "F13", {"entities" : qUnion([Q0, Q1, Q2, Q3, Q4, Q5, Q6, Q7, Q8, Q9, Q10, Q11, Q12, Q13, Q14, Q15, Q16, Q17, Q18, Q19])});
        }
        {
            var Q0;
            Q0=makeQuery(id+"F1.opExtrude","SWEPT_BODY",BODY,{"disambiguationData":[OSD([sQuery(id+"F0.wireOp",EDGE,"E0.bottom"),sQuery(id+"F0.wireOp",EDGE,"E0.top"),sQuery(id+"F0.wireOp",EDGE,"E0.left"),sQuery(id+"F0.wireOp",EDGE,"E0.right")])]});
            var Q1;
            Q1=makeQuery(id+"F7.opPattern","COPY",BODY,{"derivedFrom":makeQuery(id+"F6.opPattern","COPY",BODY,{"derivedFrom":makeQuery(id+"F5.opPattern","COPY",BODY,{"derivedFrom":makeQuery(id+"F4.opPattern","COPY",BODY,{"derivedFrom":makeQuery(id+"F1.opExtrude","SWEPT_BODY",BODY,{"disambiguationData":[OSD([sQuery(id+"F0.wireOp",EDGE,"E0.bottom"),sQuery(id+"F0.wireOp",EDGE,"E0.top"),sQuery(id+"F0.wireOp",EDGE,"E0.left"),sQuery(id+"F0.wireOp",EDGE,"E0.right")])]}),"instanceName":"1"}),"instanceName":"1"}),"instanceName":"1"}),"instanceName":"1"});
            var Q2;
            Q2=makeQuery(id+"F6.opPattern","COPY",BODY,{"derivedFrom":makeQuery(id+"F5.opPattern","COPY",BODY,{"derivedFrom":makeQuery(id+"F4.opPattern","COPY",BODY,{"derivedFrom":makeQuery(id+"F1.opExtrude","SWEPT_BODY",BODY,{"disambiguationData":[OSD([sQuery(id+"F0.wireOp",EDGE,"E0.bottom"),sQuery(id+"F0.wireOp",EDGE,"E0.top"),sQuery(id+"F0.wireOp",EDGE,"E0.left"),sQuery(id+"F0.wireOp",EDGE,"E0.right")])]}),"instanceName":"1"}),"instanceName":"1"}),"instanceName":"1"});
            var Q3;
            Q3=makeQuery(id+"F5.opPattern","COPY",BODY,{"derivedFrom":makeQuery(id+"F4.opPattern","COPY",BODY,{"derivedFrom":makeQuery(id+"F1.opExtrude","SWEPT_BODY",BODY,{"disambiguationData":[OSD([sQuery(id+"F0.wireOp",EDGE,"E0.bottom"),sQuery(id+"F0.wireOp",EDGE,"E0.top"),sQuery(id+"F0.wireOp",EDGE,"E0.left"),sQuery(id+"F0.wireOp",EDGE,"E0.right")])]}),"instanceName":"1"}),"instanceName":"1"});
            var Q4;
            Q4=makeQuery(id+"F4.opPattern","COPY",BODY,{"derivedFrom":makeQuery(id+"F1.opExtrude","SWEPT_BODY",BODY,{"disambiguationData":[OSD([sQuery(id+"F0.wireOp",EDGE,"E0.bottom"),sQuery(id+"F0.wireOp",EDGE,"E0.top"),sQuery(id+"F0.wireOp",EDGE,"E0.left"),sQuery(id+"F0.wireOp",EDGE,"E0.right")])]}),"instanceName":"1"});
            transform(context, id + "F14", {"entities" : qUnion([Q0, Q1, Q2, Q3, Q4]), "transformType" : TransformType.TRANSLATION_3D, "dx" : 0 * mm, "dy" : 0 * mm, "dz" : 53.97 * mm, "makeCopy" : true});
        }
        {
            var Q0;
            Q0=makeQuery(id+"F14.opPattern","COPY",BODY,{"derivedFrom":makeQuery(id+"F1.opExtrude","SWEPT_BODY",BODY,{"disambiguationData":[OSD([sQuery(id+"F0.wireOp",EDGE,"E0.bottom"),sQuery(id+"F0.wireOp",EDGE,"E0.top"),sQuery(id+"F0.wireOp",EDGE,"E0.left"),sQuery(id+"F0.wireOp",EDGE,"E0.right")])]}),"instanceName":"1"});
            var Q1;
            Q1=makeQuery(id+"F14.opPattern","COPY",BODY,{"derivedFrom":makeQuery(id+"F7.opPattern","COPY",BODY,{"derivedFrom":makeQuery(id+"F6.opPattern","COPY",BODY,{"derivedFrom":makeQuery(id+"F5.opPattern","COPY",BODY,{"derivedFrom":makeQuery(id+"F4.opPattern","COPY",BODY,{"derivedFrom":makeQuery(id+"F1.opExtrude","SWEPT_BODY",BODY,{"disambiguationData":[OSD([sQuery(id+"F0.wireOp",EDGE,"E0.bottom"),sQuery(id+"F0.wireOp",EDGE,"E0.top"),sQuery(id+"F0.wireOp",EDGE,"E0.left"),sQuery(id+"F0.wireOp",EDGE,"E0.right")])]}),"instanceName":"1"}),"instanceName":"1"}),"instanceName":"1"}),"instanceName":"1"}),"instanceName":"1"});
            var Q2;
            Q2=makeQuery(id+"F14.opPattern","COPY",BODY,{"derivedFrom":makeQuery(id+"F6.opPattern","COPY",BODY,{"derivedFrom":makeQuery(id+"F5.opPattern","COPY",BODY,{"derivedFrom":makeQuery(id+"F4.opPattern","COPY",BODY,{"derivedFrom":makeQuery(id+"F1.opExtrude","SWEPT_BODY",BODY,{"disambiguationData":[OSD([sQuery(id+"F0.wireOp",EDGE,"E0.bottom"),sQuery(id+"F0.wireOp",EDGE,"E0.top"),sQuery(id+"F0.wireOp",EDGE,"E0.left"),sQuery(id+"F0.wireOp",EDGE,"E0.right")])]}),"instanceName":"1"}),"instanceName":"1"}),"instanceName":"1"}),"instanceName":"1"});
            var Q3;
            Q3=makeQuery(id+"F14.opPattern","COPY",BODY,{"derivedFrom":makeQuery(id+"F5.opPattern","COPY",BODY,{"derivedFrom":makeQuery(id+"F4.opPattern","COPY",BODY,{"derivedFrom":makeQuery(id+"F1.opExtrude","SWEPT_BODY",BODY,{"disambiguationData":[OSD([sQuery(id+"F0.wireOp",EDGE,"E0.bottom"),sQuery(id+"F0.wireOp",EDGE,"E0.top"),sQuery(id+"F0.wireOp",EDGE,"E0.left"),sQuery(id+"F0.wireOp",EDGE,"E0.right")])]}),"instanceName":"1"}),"instanceName":"1"}),"instanceName":"1"});
            var Q4;
            Q4=makeQuery(id+"F14.opPattern","COPY",BODY,{"derivedFrom":makeQuery(id+"F4.opPattern","COPY",BODY,{"derivedFrom":makeQuery(id+"F1.opExtrude","SWEPT_BODY",BODY,{"disambiguationData":[OSD([sQuery(id+"F0.wireOp",EDGE,"E0.bottom"),sQuery(id+"F0.wireOp",EDGE,"E0.top"),sQuery(id+"F0.wireOp",EDGE,"E0.left"),sQuery(id+"F0.wireOp",EDGE,"E0.right")])]}),"instanceName":"1"}),"instanceName":"1"});
            transform(context, id + "F15", {"entities" : qUnion([Q0, Q1, Q2, Q3, Q4]), "transformType" : TransformType.TRANSLATION_3D, "dx" : 0 * mm, "dy" : 0 * mm, "dz" : 53.97 * mm, "makeCopy" : true});
        }
        {
            var Q0;
            Q0=makeQuery(id+"F15.opPattern","COPY",BODY,{"derivedFrom":makeQuery(id+"F14.opPattern","COPY",BODY,{"derivedFrom":makeQuery(id+"F1.opExtrude","SWEPT_BODY",BODY,{"disambiguationData":[OSD([sQuery(id+"F0.wireOp",EDGE,"E0.bottom"),sQuery(id+"F0.wireOp",EDGE,"E0.top"),sQuery(id+"F0.wireOp",EDGE,"E0.left"),sQuery(id+"F0.wireOp",EDGE,"E0.right")])]}),"instanceName":"1"}),"instanceName":"1"});
            var Q1;
            Q1=makeQuery(id+"F15.opPattern","COPY",BODY,{"derivedFrom":makeQuery(id+"F14.opPattern","COPY",BODY,{"derivedFrom":makeQuery(id+"F4.opPattern","COPY",BODY,{"derivedFrom":makeQuery(id+"F1.opExtrude","SWEPT_BODY",BODY,{"disambiguationData":[OSD([sQuery(id+"F0.wireOp",EDGE,"E0.bottom"),sQuery(id+"F0.wireOp",EDGE,"E0.top"),sQuery(id+"F0.wireOp",EDGE,"E0.left"),sQuery(id+"F0.wireOp",EDGE,"E0.right")])]}),"instanceName":"1"}),"instanceName":"1"}),"instanceName":"1"});
            var Q2;
            Q2=makeQuery(id+"F15.opPattern","COPY",BODY,{"derivedFrom":makeQuery(id+"F14.opPattern","COPY",BODY,{"derivedFrom":makeQuery(id+"F5.opPattern","COPY",BODY,{"derivedFrom":makeQuery(id+"F4.opPattern","COPY",BODY,{"derivedFrom":makeQuery(id+"F1.opExtrude","SWEPT_BODY",BODY,{"disambiguationData":[OSD([sQuery(id+"F0.wireOp",EDGE,"E0.bottom"),sQuery(id+"F0.wireOp",EDGE,"E0.top"),sQuery(id+"F0.wireOp",EDGE,"E0.left"),sQuery(id+"F0.wireOp",EDGE,"E0.right")])]}),"instanceName":"1"}),"instanceName":"1"}),"instanceName":"1"}),"instanceName":"1"});
            var Q3;
            Q3=makeQuery(id+"F15.opPattern","COPY",BODY,{"derivedFrom":makeQuery(id+"F14.opPattern","COPY",BODY,{"derivedFrom":makeQuery(id+"F6.opPattern","COPY",BODY,{"derivedFrom":makeQuery(id+"F5.opPattern","COPY",BODY,{"derivedFrom":makeQuery(id+"F4.opPattern","COPY",BODY,{"derivedFrom":makeQuery(id+"F1.opExtrude","SWEPT_BODY",BODY,{"disambiguationData":[OSD([sQuery(id+"F0.wireOp",EDGE,"E0.bottom"),sQuery(id+"F0.wireOp",EDGE,"E0.top"),sQuery(id+"F0.wireOp",EDGE,"E0.left"),sQuery(id+"F0.wireOp",EDGE,"E0.right")])]}),"instanceName":"1"}),"instanceName":"1"}),"instanceName":"1"}),"instanceName":"1"}),"instanceName":"1"});
            var Q4;
            Q4=makeQuery(id+"F15.opPattern","COPY",BODY,{"derivedFrom":makeQuery(id+"F14.opPattern","COPY",BODY,{"derivedFrom":makeQuery(id+"F7.opPattern","COPY",BODY,{"derivedFrom":makeQuery(id+"F6.opPattern","COPY",BODY,{"derivedFrom":makeQuery(id+"F5.opPattern","COPY",BODY,{"derivedFrom":makeQuery(id+"F4.opPattern","COPY",BODY,{"derivedFrom":makeQuery(id+"F1.opExtrude","SWEPT_BODY",BODY,{"disambiguationData":[OSD([sQuery(id+"F0.wireOp",EDGE,"E0.bottom"),sQuery(id+"F0.wireOp",EDGE,"E0.top"),sQuery(id+"F0.wireOp",EDGE,"E0.left"),sQuery(id+"F0.wireOp",EDGE,"E0.right")])]}),"instanceName":"1"}),"instanceName":"1"}),"instanceName":"1"}),"instanceName":"1"}),"instanceName":"1"}),"instanceName":"1"});
            transform(context, id + "F16", {"entities" : qUnion([Q0, Q1, Q2, Q3, Q4]), "transformType" : TransformType.TRANSLATION_3D, "dx" : 0 * mm, "dy" : 0 * mm, "dz" : 53.97 * mm, "makeCopy" : true});
        }
        {
            var Q0;
            Q0=makeQuery(id+"F16.opPattern","COPY",BODY,{"derivedFrom":makeQuery(id+"F15.opPattern","COPY",BODY,{"derivedFrom":makeQuery(id+"F14.opPattern","COPY",BODY,{"derivedFrom":makeQuery(id+"F1.opExtrude","SWEPT_BODY",BODY,{"disambiguationData":[OSD([sQuery(id+"F0.wireOp",EDGE,"E0.bottom"),sQuery(id+"F0.wireOp",EDGE,"E0.top"),sQuery(id+"F0.wireOp",EDGE,"E0.left"),sQuery(id+"F0.wireOp",EDGE,"E0.right")])]}),"instanceName":"1"}),"instanceName":"1"}),"instanceName":"1"});
            var Q1;
            Q1=makeQuery(id+"F16.opPattern","COPY",BODY,{"derivedFrom":makeQuery(id+"F15.opPattern","COPY",BODY,{"derivedFrom":makeQuery(id+"F14.opPattern","COPY",BODY,{"derivedFrom":makeQuery(id+"F4.opPattern","COPY",BODY,{"derivedFrom":makeQuery(id+"F1.opExtrude","SWEPT_BODY",BODY,{"disambiguationData":[OSD([sQuery(id+"F0.wireOp",EDGE,"E0.bottom"),sQuery(id+"F0.wireOp",EDGE,"E0.top"),sQuery(id+"F0.wireOp",EDGE,"E0.left"),sQuery(id+"F0.wireOp",EDGE,"E0.right")])]}),"instanceName":"1"}),"instanceName":"1"}),"instanceName":"1"}),"instanceName":"1"});
            var Q2;
            Q2=makeQuery(id+"F16.opPattern","COPY",BODY,{"derivedFrom":makeQuery(id+"F15.opPattern","COPY",BODY,{"derivedFrom":makeQuery(id+"F14.opPattern","COPY",BODY,{"derivedFrom":makeQuery(id+"F5.opPattern","COPY",BODY,{"derivedFrom":makeQuery(id+"F4.opPattern","COPY",BODY,{"derivedFrom":makeQuery(id+"F1.opExtrude","SWEPT_BODY",BODY,{"disambiguationData":[OSD([sQuery(id+"F0.wireOp",EDGE,"E0.bottom"),sQuery(id+"F0.wireOp",EDGE,"E0.top"),sQuery(id+"F0.wireOp",EDGE,"E0.left"),sQuery(id+"F0.wireOp",EDGE,"E0.right")])]}),"instanceName":"1"}),"instanceName":"1"}),"instanceName":"1"}),"instanceName":"1"}),"instanceName":"1"});
            var Q3;
            Q3=makeQuery(id+"F16.opPattern","COPY",BODY,{"derivedFrom":makeQuery(id+"F15.opPattern","COPY",BODY,{"derivedFrom":makeQuery(id+"F14.opPattern","COPY",BODY,{"derivedFrom":makeQuery(id+"F7.opPattern","COPY",BODY,{"derivedFrom":makeQuery(id+"F6.opPattern","COPY",BODY,{"derivedFrom":makeQuery(id+"F5.opPattern","COPY",BODY,{"derivedFrom":makeQuery(id+"F4.opPattern","COPY",BODY,{"derivedFrom":makeQuery(id+"F1.opExtrude","SWEPT_BODY",BODY,{"disambiguationData":[OSD([sQuery(id+"F0.wireOp",EDGE,"E0.bottom"),sQuery(id+"F0.wireOp",EDGE,"E0.top"),sQuery(id+"F0.wireOp",EDGE,"E0.left"),sQuery(id+"F0.wireOp",EDGE,"E0.right")])]}),"instanceName":"1"}),"instanceName":"1"}),"instanceName":"1"}),"instanceName":"1"}),"instanceName":"1"}),"instanceName":"1"}),"instanceName":"1"});
            var Q4;
            Q4=makeQuery(id+"F16.opPattern","COPY",BODY,{"derivedFrom":makeQuery(id+"F15.opPattern","COPY",BODY,{"derivedFrom":makeQuery(id+"F14.opPattern","COPY",BODY,{"derivedFrom":makeQuery(id+"F6.opPattern","COPY",BODY,{"derivedFrom":makeQuery(id+"F5.opPattern","COPY",BODY,{"derivedFrom":makeQuery(id+"F4.opPattern","COPY",BODY,{"derivedFrom":makeQuery(id+"F1.opExtrude","SWEPT_BODY",BODY,{"disambiguationData":[OSD([sQuery(id+"F0.wireOp",EDGE,"E0.bottom"),sQuery(id+"F0.wireOp",EDGE,"E0.top"),sQuery(id+"F0.wireOp",EDGE,"E0.left"),sQuery(id+"F0.wireOp",EDGE,"E0.right")])]}),"instanceName":"1"}),"instanceName":"1"}),"instanceName":"1"}),"instanceName":"1"}),"instanceName":"1"}),"instanceName":"1"});
            transform(context, id + "F17", {"entities" : qUnion([Q0, Q1, Q2, Q3, Q4]), "transformType" : TransformType.TRANSLATION_3D, "dx" : 0 * mm, "dy" : 0 * mm, "dz" : 53.97 * mm, "makeCopy" : true});
        }
        {
            var Q0;
            Q0=makeQuery(id+"F1.opExtrude","SWEPT_BODY",BODY,{"disambiguationData":[OSD([sQuery(id+"F0.wireOp",EDGE,"E0.bottom"),sQuery(id+"F0.wireOp",EDGE,"E0.top"),sQuery(id+"F0.wireOp",EDGE,"E0.left"),sQuery(id+"F0.wireOp",EDGE,"E0.right")])]});
            var Q1;
            Q1=makeQuery(id+"F5.opPattern","COPY",BODY,{"derivedFrom":makeQuery(id+"F4.opPattern","COPY",BODY,{"derivedFrom":makeQuery(id+"F1.opExtrude","SWEPT_BODY",BODY,{"disambiguationData":[OSD([sQuery(id+"F0.wireOp",EDGE,"E0.bottom"),sQuery(id+"F0.wireOp",EDGE,"E0.top"),sQuery(id+"F0.wireOp",EDGE,"E0.left"),sQuery(id+"F0.wireOp",EDGE,"E0.right")])]}),"instanceName":"1"}),"instanceName":"1"});
            var Q2;
            Q2=makeQuery(id+"F7.opPattern","COPY",BODY,{"derivedFrom":makeQuery(id+"F6.opPattern","COPY",BODY,{"derivedFrom":makeQuery(id+"F5.opPattern","COPY",BODY,{"derivedFrom":makeQuery(id+"F4.opPattern","COPY",BODY,{"derivedFrom":makeQuery(id+"F1.opExtrude","SWEPT_BODY",BODY,{"disambiguationData":[OSD([sQuery(id+"F0.wireOp",EDGE,"E0.bottom"),sQuery(id+"F0.wireOp",EDGE,"E0.top"),sQuery(id+"F0.wireOp",EDGE,"E0.left"),sQuery(id+"F0.wireOp",EDGE,"E0.right")])]}),"instanceName":"1"}),"instanceName":"1"}),"instanceName":"1"}),"instanceName":"1"});
            var Q3;
            Q3=makeQuery(id+"F14.opPattern","COPY",BODY,{"derivedFrom":makeQuery(id+"F6.opPattern","COPY",BODY,{"derivedFrom":makeQuery(id+"F5.opPattern","COPY",BODY,{"derivedFrom":makeQuery(id+"F4.opPattern","COPY",BODY,{"derivedFrom":makeQuery(id+"F1.opExtrude","SWEPT_BODY",BODY,{"disambiguationData":[OSD([sQuery(id+"F0.wireOp",EDGE,"E0.bottom"),sQuery(id+"F0.wireOp",EDGE,"E0.top"),sQuery(id+"F0.wireOp",EDGE,"E0.left"),sQuery(id+"F0.wireOp",EDGE,"E0.right")])]}),"instanceName":"1"}),"instanceName":"1"}),"instanceName":"1"}),"instanceName":"1"});
            var Q4;
            Q4=makeQuery(id+"F14.opPattern","COPY",BODY,{"derivedFrom":makeQuery(id+"F4.opPattern","COPY",BODY,{"derivedFrom":makeQuery(id+"F1.opExtrude","SWEPT_BODY",BODY,{"disambiguationData":[OSD([sQuery(id+"F0.wireOp",EDGE,"E0.bottom"),sQuery(id+"F0.wireOp",EDGE,"E0.top"),sQuery(id+"F0.wireOp",EDGE,"E0.left"),sQuery(id+"F0.wireOp",EDGE,"E0.right")])]}),"instanceName":"1"}),"instanceName":"1"});
            var Q5;
            Q5=makeQuery(id+"F15.opPattern","COPY",BODY,{"derivedFrom":makeQuery(id+"F14.opPattern","COPY",BODY,{"derivedFrom":makeQuery(id+"F1.opExtrude","SWEPT_BODY",BODY,{"disambiguationData":[OSD([sQuery(id+"F0.wireOp",EDGE,"E0.bottom"),sQuery(id+"F0.wireOp",EDGE,"E0.top"),sQuery(id+"F0.wireOp",EDGE,"E0.left"),sQuery(id+"F0.wireOp",EDGE,"E0.right")])]}),"instanceName":"1"}),"instanceName":"1"});
            var Q6;
            Q6=makeQuery(id+"F15.opPattern","COPY",BODY,{"derivedFrom":makeQuery(id+"F14.opPattern","COPY",BODY,{"derivedFrom":makeQuery(id+"F5.opPattern","COPY",BODY,{"derivedFrom":makeQuery(id+"F4.opPattern","COPY",BODY,{"derivedFrom":makeQuery(id+"F1.opExtrude","SWEPT_BODY",BODY,{"disambiguationData":[OSD([sQuery(id+"F0.wireOp",EDGE,"E0.bottom"),sQuery(id+"F0.wireOp",EDGE,"E0.top"),sQuery(id+"F0.wireOp",EDGE,"E0.left"),sQuery(id+"F0.wireOp",EDGE,"E0.right")])]}),"instanceName":"1"}),"instanceName":"1"}),"instanceName":"1"}),"instanceName":"1"});
            var Q7;
            Q7=makeQuery(id+"F15.opPattern","COPY",BODY,{"derivedFrom":makeQuery(id+"F14.opPattern","COPY",BODY,{"derivedFrom":makeQuery(id+"F7.opPattern","COPY",BODY,{"derivedFrom":makeQuery(id+"F6.opPattern","COPY",BODY,{"derivedFrom":makeQuery(id+"F5.opPattern","COPY",BODY,{"derivedFrom":makeQuery(id+"F4.opPattern","COPY",BODY,{"derivedFrom":makeQuery(id+"F1.opExtrude","SWEPT_BODY",BODY,{"disambiguationData":[OSD([sQuery(id+"F0.wireOp",EDGE,"E0.bottom"),sQuery(id+"F0.wireOp",EDGE,"E0.top"),sQuery(id+"F0.wireOp",EDGE,"E0.left"),sQuery(id+"F0.wireOp",EDGE,"E0.right")])]}),"instanceName":"1"}),"instanceName":"1"}),"instanceName":"1"}),"instanceName":"1"}),"instanceName":"1"}),"instanceName":"1"});
            var Q8;
            Q8=makeQuery(id+"F16.opPattern","COPY",BODY,{"derivedFrom":makeQuery(id+"F15.opPattern","COPY",BODY,{"derivedFrom":makeQuery(id+"F14.opPattern","COPY",BODY,{"derivedFrom":makeQuery(id+"F6.opPattern","COPY",BODY,{"derivedFrom":makeQuery(id+"F5.opPattern","COPY",BODY,{"derivedFrom":makeQuery(id+"F4.opPattern","COPY",BODY,{"derivedFrom":makeQuery(id+"F1.opExtrude","SWEPT_BODY",BODY,{"disambiguationData":[OSD([sQuery(id+"F0.wireOp",EDGE,"E0.bottom"),sQuery(id+"F0.wireOp",EDGE,"E0.top"),sQuery(id+"F0.wireOp",EDGE,"E0.left"),sQuery(id+"F0.wireOp",EDGE,"E0.right")])]}),"instanceName":"1"}),"instanceName":"1"}),"instanceName":"1"}),"instanceName":"1"}),"instanceName":"1"}),"instanceName":"1"});
            var Q9;
            Q9=makeQuery(id+"F16.opPattern","COPY",BODY,{"derivedFrom":makeQuery(id+"F15.opPattern","COPY",BODY,{"derivedFrom":makeQuery(id+"F14.opPattern","COPY",BODY,{"derivedFrom":makeQuery(id+"F4.opPattern","COPY",BODY,{"derivedFrom":makeQuery(id+"F1.opExtrude","SWEPT_BODY",BODY,{"disambiguationData":[OSD([sQuery(id+"F0.wireOp",EDGE,"E0.bottom"),sQuery(id+"F0.wireOp",EDGE,"E0.top"),sQuery(id+"F0.wireOp",EDGE,"E0.left"),sQuery(id+"F0.wireOp",EDGE,"E0.right")])]}),"instanceName":"1"}),"instanceName":"1"}),"instanceName":"1"}),"instanceName":"1"});
            var Q10;
            Q10=makeQuery(id+"F17.opPattern","COPY",BODY,{"derivedFrom":makeQuery(id+"F16.opPattern","COPY",BODY,{"derivedFrom":makeQuery(id+"F15.opPattern","COPY",BODY,{"derivedFrom":makeQuery(id+"F14.opPattern","COPY",BODY,{"derivedFrom":makeQuery(id+"F1.opExtrude","SWEPT_BODY",BODY,{"disambiguationData":[OSD([sQuery(id+"F0.wireOp",EDGE,"E0.bottom"),sQuery(id+"F0.wireOp",EDGE,"E0.top"),sQuery(id+"F0.wireOp",EDGE,"E0.left"),sQuery(id+"F0.wireOp",EDGE,"E0.right")])]}),"instanceName":"1"}),"instanceName":"1"}),"instanceName":"1"}),"instanceName":"1"});
            var Q11;
            Q11=makeQuery(id+"F17.opPattern","COPY",BODY,{"derivedFrom":makeQuery(id+"F16.opPattern","COPY",BODY,{"derivedFrom":makeQuery(id+"F15.opPattern","COPY",BODY,{"derivedFrom":makeQuery(id+"F14.opPattern","COPY",BODY,{"derivedFrom":makeQuery(id+"F5.opPattern","COPY",BODY,{"derivedFrom":makeQuery(id+"F4.opPattern","COPY",BODY,{"derivedFrom":makeQuery(id+"F1.opExtrude","SWEPT_BODY",BODY,{"disambiguationData":[OSD([sQuery(id+"F0.wireOp",EDGE,"E0.bottom"),sQuery(id+"F0.wireOp",EDGE,"E0.top"),sQuery(id+"F0.wireOp",EDGE,"E0.left"),sQuery(id+"F0.wireOp",EDGE,"E0.right")])]}),"instanceName":"1"}),"instanceName":"1"}),"instanceName":"1"}),"instanceName":"1"}),"instanceName":"1"}),"instanceName":"1"});
            var Q12;
            Q12=makeQuery(id+"F17.opPattern","COPY",BODY,{"derivedFrom":makeQuery(id+"F16.opPattern","COPY",BODY,{"derivedFrom":makeQuery(id+"F15.opPattern","COPY",BODY,{"derivedFrom":makeQuery(id+"F14.opPattern","COPY",BODY,{"derivedFrom":makeQuery(id+"F7.opPattern","COPY",BODY,{"derivedFrom":makeQuery(id+"F6.opPattern","COPY",BODY,{"derivedFrom":makeQuery(id+"F5.opPattern","COPY",BODY,{"derivedFrom":makeQuery(id+"F4.opPattern","COPY",BODY,{"derivedFrom":makeQuery(id+"F1.opExtrude","SWEPT_BODY",BODY,{"disambiguationData":[OSD([sQuery(id+"F0.wireOp",EDGE,"E0.bottom"),sQuery(id+"F0.wireOp",EDGE,"E0.top"),sQuery(id+"F0.wireOp",EDGE,"E0.left"),sQuery(id+"F0.wireOp",EDGE,"E0.right")])]}),"instanceName":"1"}),"instanceName":"1"}),"instanceName":"1"}),"instanceName":"1"}),"instanceName":"1"}),"instanceName":"1"}),"instanceName":"1"}),"instanceName":"1"});
            deleteBodies(context, id + "F18", {"entities" : qUnion([Q0, Q1, Q2, Q3, Q4, Q5, Q6, Q7, Q8, Q9, Q10, Q11, Q12])});
        }
        {
            var Q0;
            Q0=makeQuery(id+"F15.opPattern","COPY",BODY,{"derivedFrom":makeQuery(id+"F14.opPattern","COPY",BODY,{"derivedFrom":makeQuery(id+"F6.opPattern","COPY",BODY,{"derivedFrom":makeQuery(id+"F5.opPattern","COPY",BODY,{"derivedFrom":makeQuery(id+"F4.opPattern","COPY",BODY,{"derivedFrom":makeQuery(id+"F1.opExtrude","SWEPT_BODY",BODY,{"disambiguationData":[OSD([sQuery(id+"F0.wireOp",EDGE,"E0.bottom"),sQuery(id+"F0.wireOp",EDGE,"E0.top"),sQuery(id+"F0.wireOp",EDGE,"E0.left"),sQuery(id+"F0.wireOp",EDGE,"E0.right")])]}),"instanceName":"1"}),"instanceName":"1"}),"instanceName":"1"}),"instanceName":"1"}),"instanceName":"1"});
            var Q1;
            Q1=makeQuery(id+"F14.opPattern","COPY",BODY,{"derivedFrom":makeQuery(id+"F5.opPattern","COPY",BODY,{"derivedFrom":makeQuery(id+"F4.opPattern","COPY",BODY,{"derivedFrom":makeQuery(id+"F1.opExtrude","SWEPT_BODY",BODY,{"disambiguationData":[OSD([sQuery(id+"F0.wireOp",EDGE,"E0.bottom"),sQuery(id+"F0.wireOp",EDGE,"E0.top"),sQuery(id+"F0.wireOp",EDGE,"E0.left"),sQuery(id+"F0.wireOp",EDGE,"E0.right")])]}),"instanceName":"1"}),"instanceName":"1"}),"instanceName":"1"});
            var Q2;
            Q2=makeQuery(id+"F14.opPattern","COPY",BODY,{"derivedFrom":makeQuery(id+"F7.opPattern","COPY",BODY,{"derivedFrom":makeQuery(id+"F6.opPattern","COPY",BODY,{"derivedFrom":makeQuery(id+"F5.opPattern","COPY",BODY,{"derivedFrom":makeQuery(id+"F4.opPattern","COPY",BODY,{"derivedFrom":makeQuery(id+"F1.opExtrude","SWEPT_BODY",BODY,{"disambiguationData":[OSD([sQuery(id+"F0.wireOp",EDGE,"E0.bottom"),sQuery(id+"F0.wireOp",EDGE,"E0.top"),sQuery(id+"F0.wireOp",EDGE,"E0.left"),sQuery(id+"F0.wireOp",EDGE,"E0.right")])]}),"instanceName":"1"}),"instanceName":"1"}),"instanceName":"1"}),"instanceName":"1"}),"instanceName":"1"});
            var Q3;
            Q3=makeQuery(id+"F6.opPattern","COPY",BODY,{"derivedFrom":makeQuery(id+"F5.opPattern","COPY",BODY,{"derivedFrom":makeQuery(id+"F4.opPattern","COPY",BODY,{"derivedFrom":makeQuery(id+"F1.opExtrude","SWEPT_BODY",BODY,{"disambiguationData":[OSD([sQuery(id+"F0.wireOp",EDGE,"E0.bottom"),sQuery(id+"F0.wireOp",EDGE,"E0.top"),sQuery(id+"F0.wireOp",EDGE,"E0.left"),sQuery(id+"F0.wireOp",EDGE,"E0.right")])]}),"instanceName":"1"}),"instanceName":"1"}),"instanceName":"1"});
            var Q4;
            Q4=makeQuery(id+"F17.opPattern","COPY",BODY,{"derivedFrom":makeQuery(id+"F16.opPattern","COPY",BODY,{"derivedFrom":makeQuery(id+"F15.opPattern","COPY",BODY,{"derivedFrom":makeQuery(id+"F14.opPattern","COPY",BODY,{"derivedFrom":makeQuery(id+"F6.opPattern","COPY",BODY,{"derivedFrom":makeQuery(id+"F5.opPattern","COPY",BODY,{"derivedFrom":makeQuery(id+"F4.opPattern","COPY",BODY,{"derivedFrom":makeQuery(id+"F1.opExtrude","SWEPT_BODY",BODY,{"disambiguationData":[OSD([sQuery(id+"F0.wireOp",EDGE,"E0.bottom"),sQuery(id+"F0.wireOp",EDGE,"E0.top"),sQuery(id+"F0.wireOp",EDGE,"E0.left"),sQuery(id+"F0.wireOp",EDGE,"E0.right")])]}),"instanceName":"1"}),"instanceName":"1"}),"instanceName":"1"}),"instanceName":"1"}),"instanceName":"1"}),"instanceName":"1"}),"instanceName":"1"});
            var Q5;
            Q5=makeQuery(id+"F16.opPattern","COPY",BODY,{"derivedFrom":makeQuery(id+"F15.opPattern","COPY",BODY,{"derivedFrom":makeQuery(id+"F14.opPattern","COPY",BODY,{"derivedFrom":makeQuery(id+"F5.opPattern","COPY",BODY,{"derivedFrom":makeQuery(id+"F4.opPattern","COPY",BODY,{"derivedFrom":makeQuery(id+"F1.opExtrude","SWEPT_BODY",BODY,{"disambiguationData":[OSD([sQuery(id+"F0.wireOp",EDGE,"E0.bottom"),sQuery(id+"F0.wireOp",EDGE,"E0.top"),sQuery(id+"F0.wireOp",EDGE,"E0.left"),sQuery(id+"F0.wireOp",EDGE,"E0.right")])]}),"instanceName":"1"}),"instanceName":"1"}),"instanceName":"1"}),"instanceName":"1"}),"instanceName":"1"});
            var Q6;
            Q6=makeQuery(id+"F16.opPattern","COPY",BODY,{"derivedFrom":makeQuery(id+"F15.opPattern","COPY",BODY,{"derivedFrom":makeQuery(id+"F14.opPattern","COPY",BODY,{"derivedFrom":makeQuery(id+"F7.opPattern","COPY",BODY,{"derivedFrom":makeQuery(id+"F6.opPattern","COPY",BODY,{"derivedFrom":makeQuery(id+"F5.opPattern","COPY",BODY,{"derivedFrom":makeQuery(id+"F4.opPattern","COPY",BODY,{"derivedFrom":makeQuery(id+"F1.opExtrude","SWEPT_BODY",BODY,{"disambiguationData":[OSD([sQuery(id+"F0.wireOp",EDGE,"E0.bottom"),sQuery(id+"F0.wireOp",EDGE,"E0.top"),sQuery(id+"F0.wireOp",EDGE,"E0.left"),sQuery(id+"F0.wireOp",EDGE,"E0.right")])]}),"instanceName":"1"}),"instanceName":"1"}),"instanceName":"1"}),"instanceName":"1"}),"instanceName":"1"}),"instanceName":"1"}),"instanceName":"1"});
            var Q7;
            Q7=makeQuery(id+"F14.opPattern","COPY",BODY,{"derivedFrom":makeQuery(id+"F1.opExtrude","SWEPT_BODY",BODY,{"disambiguationData":[OSD([sQuery(id+"F0.wireOp",EDGE,"E0.bottom"),sQuery(id+"F0.wireOp",EDGE,"E0.top"),sQuery(id+"F0.wireOp",EDGE,"E0.left"),sQuery(id+"F0.wireOp",EDGE,"E0.right")])]}),"instanceName":"1"});
            var Q8;
            Q8=makeQuery(id+"F16.opPattern","COPY",BODY,{"derivedFrom":makeQuery(id+"F15.opPattern","COPY",BODY,{"derivedFrom":makeQuery(id+"F14.opPattern","COPY",BODY,{"derivedFrom":makeQuery(id+"F1.opExtrude","SWEPT_BODY",BODY,{"disambiguationData":[OSD([sQuery(id+"F0.wireOp",EDGE,"E0.bottom"),sQuery(id+"F0.wireOp",EDGE,"E0.top"),sQuery(id+"F0.wireOp",EDGE,"E0.left"),sQuery(id+"F0.wireOp",EDGE,"E0.right")])]}),"instanceName":"1"}),"instanceName":"1"}),"instanceName":"1"});
            deleteBodies(context, id + "F19", {"entities" : qUnion([Q0, Q1, Q2, Q3, Q4, Q5, Q6, Q7, Q8])});
        }
        {
            var Q0;
            Q0=makeQuery(id+"F17.opPattern","COPY",BODY,{"derivedFrom":makeQuery(id+"F16.opPattern","COPY",BODY,{"derivedFrom":makeQuery(id+"F15.opPattern","COPY",BODY,{"derivedFrom":makeQuery(id+"F14.opPattern","COPY",BODY,{"derivedFrom":makeQuery(id+"F4.opPattern","COPY",BODY,{"derivedFrom":makeQuery(id+"F1.opExtrude","SWEPT_BODY",BODY,{"disambiguationData":[OSD([sQuery(id+"F0.wireOp",EDGE,"E0.bottom"),sQuery(id+"F0.wireOp",EDGE,"E0.top"),sQuery(id+"F0.wireOp",EDGE,"E0.left"),sQuery(id+"F0.wireOp",EDGE,"E0.right")])]}),"instanceName":"1"}),"instanceName":"1"}),"instanceName":"1"}),"instanceName":"1"}),"instanceName":"1"});
            deleteBodies(context, id + "F20", {"entities" : qUnion([Q0])});
        }
    });
